# Revit family: axor_angle_valve_with_cover_51307000
name_source: partatom
category: Plumbing Fixtures
revit_build: Autodesk Revit 2015 (Build: 20140903_1530(x64)
units: mm (PartAtom-declared; Revit-internal decimal feet)

## types (1)
- Chrome 000
    BIMobject category = Other
    BOSUseNativeGeometries = 1
    Default Elevation = 4' - 0"
    Design country = Germany
    EAN code = https://4059625079263
    Edition number = 1
    IFC Classification = Sanitary Terminal
    Installation instructions = https://pro.hansgrohe-int.com
    Manufacturer country = Germany
    Manufacturer name = AXOR
    Material main = Chrome
    NBS Reference Code = 35-65-70-75
    NBS Reference Description = Sanitary Accessory Systems
    Nominal height = 0
    Nominal width = 0
    OmniClass Code = 23-27 31 00
    OmniClass Description = Valves
    Product Guid = 30aa38d9-98f9-4e5d-aa9f-f6aea05b6e66
    Product SKU = 51307000
    Product data url = https://bimobject.com
    Product family = Wastes and overflows
    Product group = Traps
    Product name = AXOR Angle valve with cover 51307000
    Product url = https://pro.hansgrohe-int.com
    QR code = http://bimobject.com
    Technical description = https://pro.hansgrohe-int.com
    Uniclass 1.4 Code = L721
    Uniclass 1.4 Description = Sanitary equipment
    Uniclass 2.0 Code = PR-31-75
    Uniclass 2.0 Description = Sanitary Accessories
    Uniclass 2015 Code = Ss_40_15_75_75
    Uniclass 2015 Name = Sanitary accessory systems
    Uniformat II Code = D2010
    Uniformat II Description = Plumbing Fixtures
    Weight Net (Kg) = 0

## geometry (parser evidence)
native form markers: Sweep x2
no freeform markers — native parametric forms only
